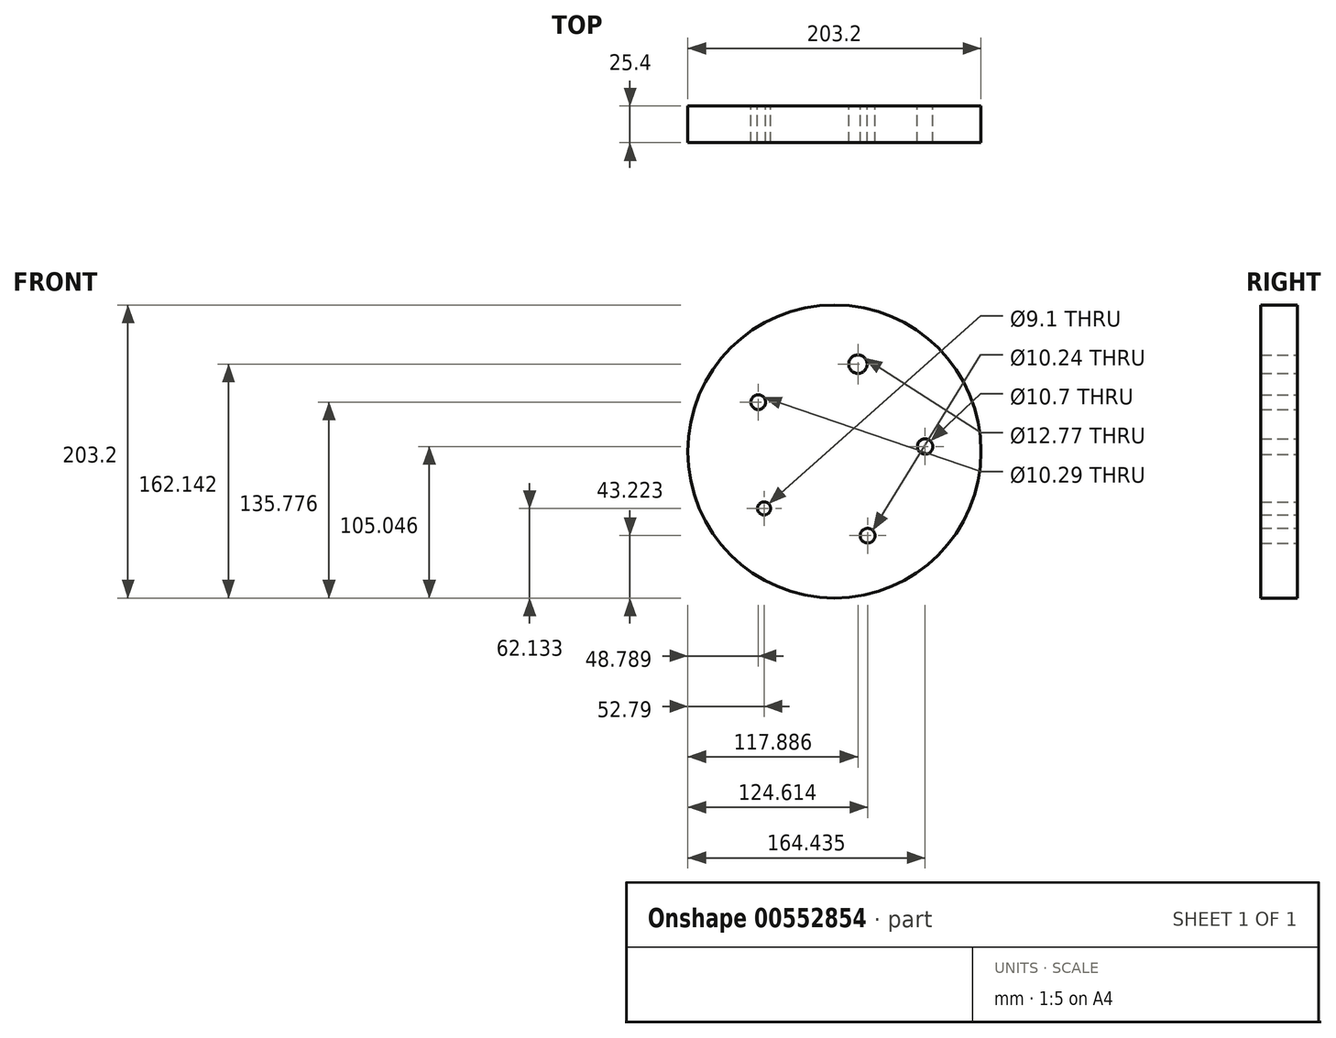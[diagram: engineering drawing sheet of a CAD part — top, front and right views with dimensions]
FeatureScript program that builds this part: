
annotation { "Feature Type Name" : "Feature", "Feature Type Description" : "" }
export const myFeature = defineFeature(function(context is Context, id is Id, definition is map)
    precondition{}
    {
        {
            var Q0;
            Q0=qCreatedBy(makeId("Front.planeOp"),FACE);
            var sketch = newSketch(context, id + "F0", { "sketchPlane" : qUnion([Q0])});
            skCircle(sketch, "E0", {"center": v(-34.27, 12.4) * mm, "radius": 101.6 * mm});
            skSolve(sketch);
        }
        {
            var Q0;
            Q0=makeQuery(id+"F0.imprint","IMPRINT",FACE,{"disambiguationData":[TD([[makeQuery(id+"F0.imprint","IMPRINT",EDGE,{"derivedFrom":sQuery(id+"F0.wireOp",EDGE,"E0")}),1.0]])]});
            var sketch = newSketch(context, id + "F1", { "sketchPlane" : qUnion([Q0])});
            skCircle(sketch, "E1", {"center": v(-87.08, 46.59) * mm, "radius": 5.14 * mm});
            skCircle(sketch, "E2", {"center": v(-17.98, 72.95) * mm, "radius": 6.39 * mm});
            skCircle(sketch, "E3", {"center": v(28.57, 15.86) * mm, "radius": 5.35 * mm});
            skCircle(sketch, "E4", {"center": v(-11.26, -45.97) * mm, "radius": 5.12 * mm});
            skCircle(sketch, "E5", {"center": v(-83.08, -27.06) * mm, "radius": 4.55 * mm});
            skSolve(sketch);
        }
        {
            var Q0;
            Q0=sQuery(id+"F0.wireOp",EDGE,"E0");
            extrude(context, id + "F2", {"bodyType" : ToolBodyType.SURFACE, "surfaceEntities" : qUnion([Q0]), "depth" : 25.4 * mm, "offsetDistance" : 25.4 * mm});
        }
        {
            var Q0;
            Q0=makeQuery(id+"F1.imprint","IMPRINT",FACE,{"disambiguationData":[TD([[makeQuery(id+"F1.imprint","IMPRINT",EDGE,{"derivedFrom":sQuery(id+"F1.wireOp",EDGE,"E1")}),-1.0]])]});
            extrude(context, id + "F3", {"entities" : qUnion([Q0]), "depth" : 25.4 * mm, "offsetDistance" : 25.4 * mm});
        }
    });
